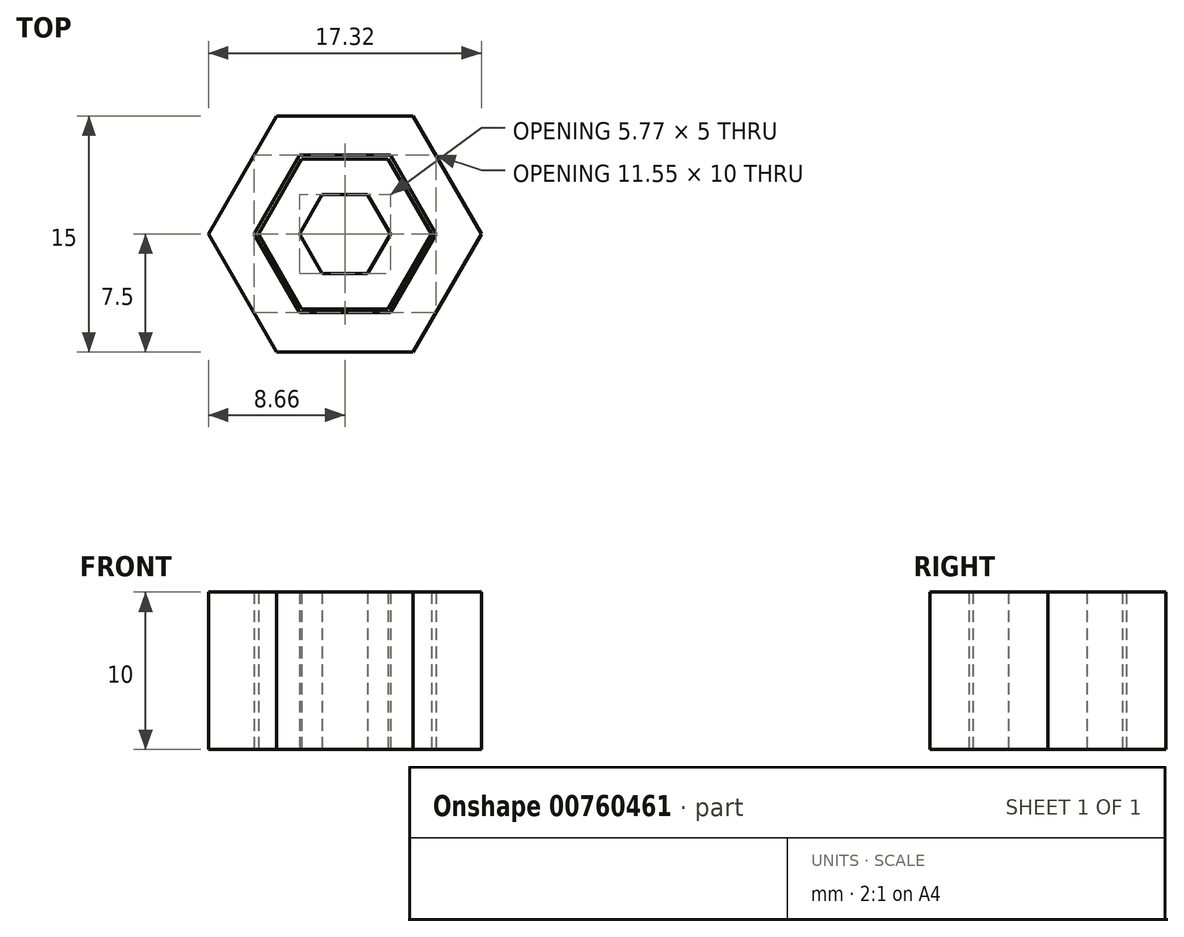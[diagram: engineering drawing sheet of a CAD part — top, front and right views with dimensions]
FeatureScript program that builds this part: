
annotation { "Feature Type Name" : "Feature", "Feature Type Description" : "" }
export const myFeature = defineFeature(function(context is Context, id is Id, definition is map)
    precondition{}
    {
        {
            var Q0;
            Q0=qCreatedBy(makeId("Top.planeOp"),FACE);
            var sketch = newSketch(context, id + "F0", { "sketchPlane" : qUnion([Q0])});
            skCircle(sketch, "E0.cCircle", {"center": v(0, 0) * mm, "radius": 4.75 * mm, "construction": true});
            skLineSegment(sketch, "E0.0", {"start": v(-2.74, 4.75) * mm, "end": v(2.74, 4.75) * mm});
            skLineSegment(sketch, "E0.1", {"start": v(2.74, 4.75) * mm, "end": v(5.48, 0) * mm});
            skLineSegment(sketch, "E0.2", {"start": v(5.48, 0) * mm, "end": v(2.74, -4.75) * mm});
            skLineSegment(sketch, "E0.3", {"start": v(2.74, -4.75) * mm, "end": v(-2.74, -4.75) * mm});
            skLineSegment(sketch, "E0.4", {"start": v(-2.74, -4.75) * mm, "end": v(-5.48, 0) * mm});
            skLineSegment(sketch, "E0.5", {"start": v(-5.48, 0) * mm, "end": v(-2.74, 4.75) * mm});
            skPoint(sketch, "E0.0.midPoint", {"position": v(0, 4.75) * mm});
            skCircle(sketch, "E1.cCircle", {"center": v(0, 0) * mm, "radius": 5 * mm, "construction": true});
            skLineSegment(sketch, "E1.0", {"start": v(-2.89, 5) * mm, "end": v(2.89, 5) * mm});
            skLineSegment(sketch, "E1.1", {"start": v(2.89, 5) * mm, "end": v(5.77, 0) * mm});
            skLineSegment(sketch, "E1.2", {"start": v(5.77, 0) * mm, "end": v(2.89, -5) * mm});
            skLineSegment(sketch, "E1.3", {"start": v(2.89, -5) * mm, "end": v(-2.89, -5) * mm});
            skLineSegment(sketch, "E1.4", {"start": v(-2.89, -5) * mm, "end": v(-5.77, 0) * mm});
            skLineSegment(sketch, "E1.5", {"start": v(-5.77, 0) * mm, "end": v(-2.89, 5) * mm});
            skPoint(sketch, "E1.0.midPoint", {"position": v(0, 5) * mm});
            skCircle(sketch, "E2.cCircle", {"center": v(0, 0) * mm, "radius": 7.5 * mm, "construction": true});
            skLineSegment(sketch, "E2.0", {"start": v(-4.33, 7.5) * mm, "end": v(4.33, 7.5) * mm});
            skLineSegment(sketch, "E2.1", {"start": v(4.33, 7.5) * mm, "end": v(8.66, 0) * mm});
            skLineSegment(sketch, "E2.2", {"start": v(8.66, 0) * mm, "end": v(4.33, -7.5) * mm});
            skLineSegment(sketch, "E2.3", {"start": v(4.33, -7.5) * mm, "end": v(-4.33, -7.5) * mm});
            skLineSegment(sketch, "E2.4", {"start": v(-4.33, -7.5) * mm, "end": v(-8.66, 0) * mm});
            skLineSegment(sketch, "E2.5", {"start": v(-8.66, 0) * mm, "end": v(-4.33, 7.5) * mm});
            skPoint(sketch, "E2.0.midPoint", {"position": v(0, 7.5) * mm});
            skCircle(sketch, "E3.cCircle", {"center": v(0, 0) * mm, "radius": 2.5 * mm, "construction": true});
            skLineSegment(sketch, "E3.0", {"start": v(-1.44, 2.5) * mm, "end": v(1.44, 2.5) * mm});
            skLineSegment(sketch, "E3.1", {"start": v(1.44, 2.5) * mm, "end": v(2.89, 0) * mm});
            skLineSegment(sketch, "E3.2", {"start": v(2.89, 0) * mm, "end": v(1.44, -2.5) * mm});
            skLineSegment(sketch, "E3.3", {"start": v(1.44, -2.5) * mm, "end": v(-1.44, -2.5) * mm});
            skLineSegment(sketch, "E3.4", {"start": v(-1.44, -2.5) * mm, "end": v(-2.89, 0) * mm});
            skLineSegment(sketch, "E3.5", {"start": v(-2.89, 0) * mm, "end": v(-1.44, 2.5) * mm});
            skPoint(sketch, "E3.0.midPoint", {"position": v(0, 2.5) * mm});
            skSolve(sketch);
        }
        {
            var Q0;
            Q0=makeQuery(id+"F0.imprint","IMPRINT",FACE,{"disambiguationData":[TD([[makeQuery(id+"F0.imprint","IMPRINT",EDGE,{"derivedFrom":sQuery(id+"F0.wireOp",EDGE,"E0.0")}),-1.0]])]});
            var Q1;
            Q1=makeQuery(id+"F0.imprint","IMPRINT",FACE,{"disambiguationData":[TD([[makeQuery(id+"F0.imprint","IMPRINT",EDGE,{"derivedFrom":sQuery(id+"F0.wireOp",EDGE,"E1.0")}),1.0]])]});
            extrude(context, id + "F1", {"entities" : qUnion([Q0, Q1]), "depth" : 10 * mm, "offsetDistance" : 25 * mm});
        }
    });
